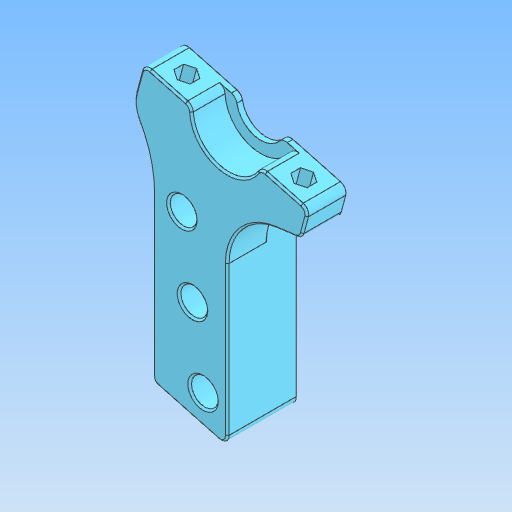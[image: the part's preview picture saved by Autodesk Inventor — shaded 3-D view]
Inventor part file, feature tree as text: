
AUTODESK INVENTOR PART (.ipt)
format: ipt  version: 2021.2 (Build 252289000, 289)  size: 367,616 bytes
history: native  units: mm
features: other x4, fillet x2, chamfer x2
ambient origin geometry x8: Origin, YZ Plane, XZ Plane, XY Plane, X Axis, Y Axis, Z Axis, Center Point
bodies: Body1 (feature_tree)
feature tree (8):
  other  "Твёрдое тело.ipt"
  fillet  "Сопряжение1"  Radius=10.0mm
  fillet  "Сопряжение2"  Radius=2.0mm
  chamfer  "Фаска1"  Distance=2.0mm
  chamfer  "Фаска2"  Distance=2.0mm Angle=45.0deg
  other  "Ножка правая верх::Твёрдое тело.ipt"
  other  "Элемент создания тегов1"
  other  "Твердое тело1"
